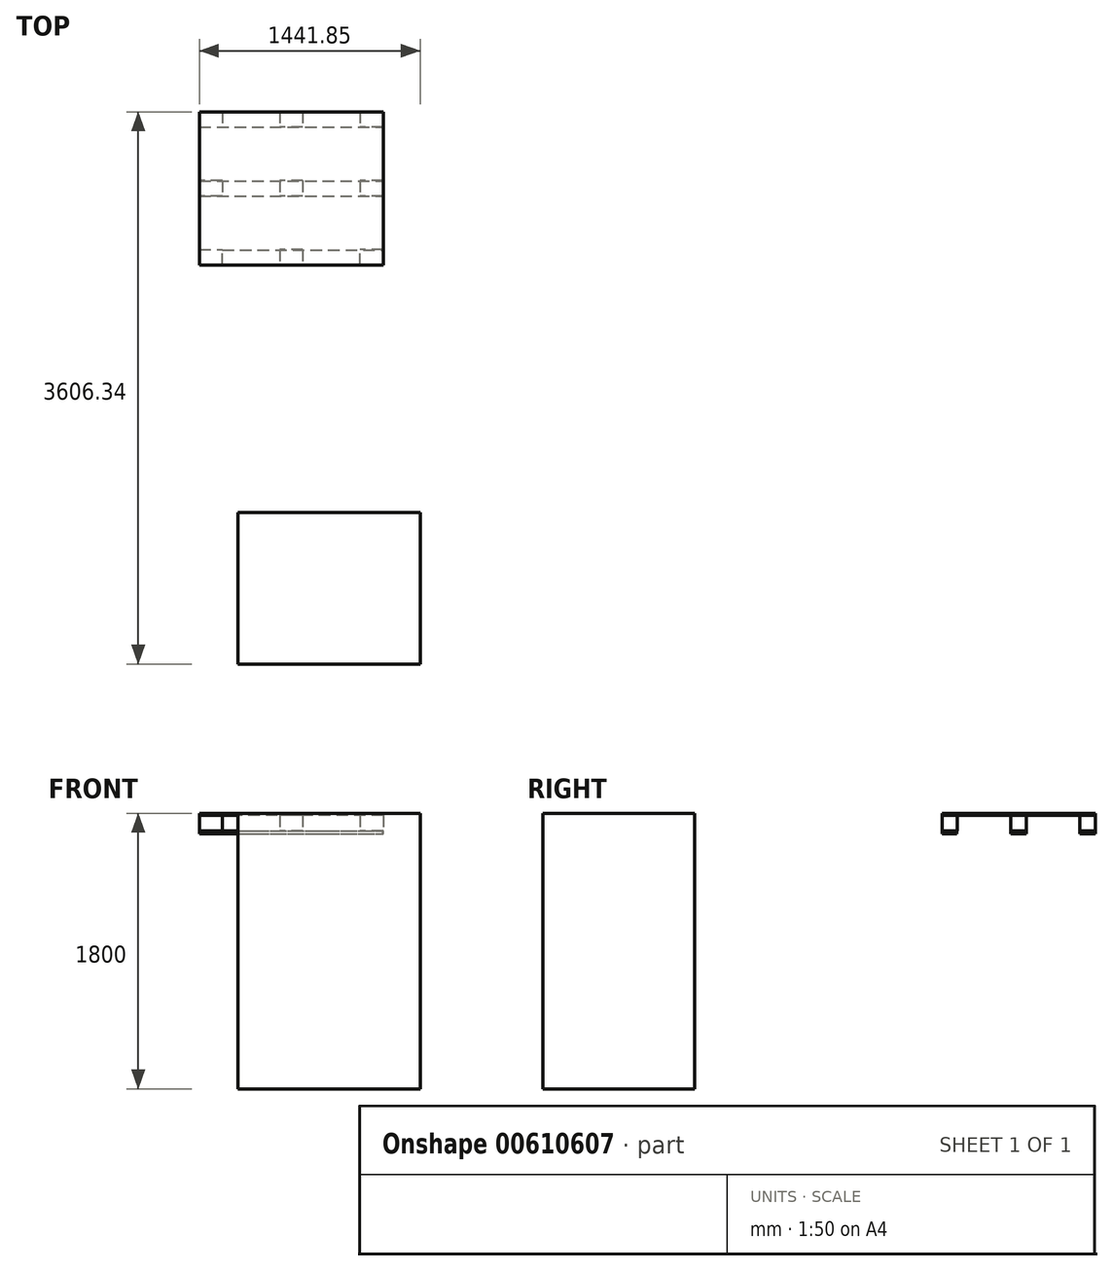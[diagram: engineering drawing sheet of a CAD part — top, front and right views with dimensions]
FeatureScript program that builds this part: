
annotation { "Feature Type Name" : "Feature", "Feature Type Description" : "" }
export const myFeature = defineFeature(function(context is Context, id is Id, definition is map)
    precondition{}
    {
        {
            var Q0;
            Q0=qCreatedBy(makeId("Top.planeOp"),FACE);
            var sketch = newSketch(context, id + "F0", { "sketchPlane" : qUnion([Q0])});
            skLineSegment(sketch, "E0.bottom", {"start": v(600, 500) * mm, "end": v(450, 500) * mm});
            skLineSegment(sketch, "E0.top", {"start": v(600, -500) * mm, "end": v(450, -500) * mm});
            skLineSegment(sketch, "E0.left", {"start": v(600, 500) * mm, "end": v(600, 400) * mm});
            skLineSegment(sketch, "E0.right", {"start": v(-600, 500) * mm, "end": v(-600, 400) * mm});
            skPoint(sketch, "E0.middle", {"position": v(0, 0) * mm});
            skLineSegment(sketch, "E1.bottom", {"start": v(-600, 500) * mm, "end": v(-450, 500) * mm});
            skLineSegment(sketch, "E1.top", {"start": v(-600, 400) * mm, "end": v(-450, 400) * mm});
            skLineSegment(sketch, "E1.right", {"start": v(-450, 500) * mm, "end": v(-450, 400) * mm});
            skLineSegment(sketch, "E2.bottom", {"start": v(-450, 50) * mm, "end": v(-600, 50) * mm});
            skLineSegment(sketch, "E2.top", {"start": v(-450, -50) * mm, "end": v(-600, -50) * mm});
            skLineSegment(sketch, "E2.left", {"start": v(-450, 50) * mm, "end": v(-450, -50) * mm});
            skPoint(sketch, "E2.middle", {"position": v(-600, 0) * mm});
            skLineSegment(sketch, "E3.bottom", {"start": v(600, 50) * mm, "end": v(450, 50) * mm});
            skLineSegment(sketch, "E3.top", {"start": v(600, -50) * mm, "end": v(450, -50) * mm});
            skLineSegment(sketch, "E3.right", {"start": v(450, 50) * mm, "end": v(450, -50) * mm});
            skPoint(sketch, "E3.middle", {"position": v(600, 0) * mm});
            skLineSegment(sketch, "E4.top", {"start": v(75, 400) * mm, "end": v(-75, 400) * mm});
            skLineSegment(sketch, "E4.left", {"start": v(75, 500) * mm, "end": v(75, 400) * mm});
            skLineSegment(sketch, "E4.right", {"start": v(-75, 500) * mm, "end": v(-75, 400) * mm});
            skPoint(sketch, "E4.middle", {"position": v(0, 500) * mm});
            skLineSegment(sketch, "E5.bottom", {"start": v(75, -400) * mm, "end": v(-75, -400) * mm});
            skLineSegment(sketch, "E5.left", {"start": v(75, -400) * mm, "end": v(75, -500) * mm});
            skLineSegment(sketch, "E5.right", {"start": v(-75, -400) * mm, "end": v(-75, -500) * mm});
            skPoint(sketch, "E5.middle", {"position": v(0, -500) * mm});
            skLineSegment(sketch, "E6.bottom", {"start": v(75, 50) * mm, "end": v(-75, 50) * mm});
            skLineSegment(sketch, "E6.top", {"start": v(75, -50) * mm, "end": v(-75, -50) * mm});
            skLineSegment(sketch, "E6.left", {"start": v(75, 50) * mm, "end": v(75, -50) * mm});
            skLineSegment(sketch, "E6.right", {"start": v(-75, 50) * mm, "end": v(-75, -50) * mm});
            skLineSegment(sketch, "E7.bottom", {"start": v(-600, -500) * mm, "end": v(-450, -500) * mm});
            skLineSegment(sketch, "E7.top", {"start": v(-600, -400) * mm, "end": v(-450, -400) * mm});
            skLineSegment(sketch, "E7.left", {"start": v(-600, -500) * mm, "end": v(-600, -400) * mm});
            skLineSegment(sketch, "E7.right", {"start": v(-450, -500) * mm, "end": v(-450, -400) * mm});
            skLineSegment(sketch, "E8.top", {"start": v(600, -400) * mm, "end": v(450, -400) * mm});
            skLineSegment(sketch, "E8.left", {"start": v(600, -500) * mm, "end": v(600, -400) * mm});
            skLineSegment(sketch, "E8.right", {"start": v(450, -500) * mm, "end": v(450, -400) * mm});
            skLineSegment(sketch, "E9.top", {"start": v(600, 400) * mm, "end": v(450, 400) * mm});
            skLineSegment(sketch, "E9.right", {"start": v(450, 500) * mm, "end": v(450, 400) * mm});
            skPoint(sketch, "E3.left.end.orphan", {"position": v(750, -50) * mm});
            skPoint(sketch, "E3.left.start.orphan", {"position": v(750, 50) * mm});
            skPoint(sketch, "E4.bottom.start.orphan", {"position": v(75, 600) * mm});
            skPoint(sketch, "E10.orphan", {"position": v(-75, 600) * mm});
            skPoint(sketch, "E2.right.start.orphan", {"position": v(-750, 50) * mm});
            skPoint(sketch, "E11.orphan", {"position": v(-750, -50) * mm});
            skPoint(sketch, "E5.top.end.orphan", {"position": v(-75, -600) * mm});
            skPoint(sketch, "E12.orphan", {"position": v(75, -600) * mm});
            skLineSegment(sketch, "E13.trimOffspring", {"start": v(-450, 500) * mm, "end": v(-600, 500) * mm});
            skLineSegment(sketch, "E14.trimOffspring", {"start": v(75, 500) * mm, "end": v(-75, 500) * mm});
            skLineSegment(sketch, "E15.trimOffspring", {"start": v(600, 50) * mm, "end": v(600, -50) * mm});
            skLineSegment(sketch, "E16.trimOffspring", {"start": v(600, -400) * mm, "end": v(600, -500) * mm});
            skLineSegment(sketch, "E17.trimOffspring", {"start": v(75, -500) * mm, "end": v(-75, -500) * mm});
            skLineSegment(sketch, "E18.trimOffspring", {"start": v(-450, -500) * mm, "end": v(-600, -500) * mm});
            skLineSegment(sketch, "E19.trimOffspring", {"start": v(-600, 50) * mm, "end": v(-600, -50) * mm});
            skLineSegment(sketch, "E20.trimOffspring", {"start": v(-600, -400) * mm, "end": v(-600, -500) * mm});
            skSolve(sketch);
        }
        {
            var Q0;
            Q0=makeQuery(id+"F0.imprint","IMPRINT",FACE,{"disambiguationData":[TD([[makeQuery(id+"F0.imprint","IMPRINT",EDGE,{"derivedFrom":sQuery(id+"F0.wireOp",EDGE,"E5.bottom")}),1.0]])]});
            var Q1;
            Q1=makeQuery(id+"F0.imprint","IMPRINT",FACE,{"disambiguationData":[TD([[makeQuery(id+"F0.imprint","IMPRINT",EDGE,{"derivedFrom":sQuery(id+"F0.wireOp",EDGE,"E7.top")}),-1.0]])]});
            var Q2;
            Q2=makeQuery(id+"F0.imprint","IMPRINT",FACE,{"disambiguationData":[TD([[makeQuery(id+"F0.imprint","IMPRINT",EDGE,{"derivedFrom":sQuery(id+"F0.wireOp",EDGE,"E2.bottom")}),1.0]])]});
            var Q3;
            Q3=makeQuery(id+"F0.imprint","IMPRINT",FACE,{"disambiguationData":[TD([[makeQuery(id+"F0.imprint","IMPRINT",EDGE,{"derivedFrom":sQuery(id+"F0.wireOp",EDGE,"E1.top")}),1.0]])]});
            var Q4;
            Q4=makeQuery(id+"F0.imprint","IMPRINT",FACE,{"disambiguationData":[TD([[makeQuery(id+"F0.imprint","IMPRINT",EDGE,{"derivedFrom":sQuery(id+"F0.wireOp",EDGE,"E4.top")}),-1.0]])]});
            var Q5;
            Q5=makeQuery(id+"F0.imprint","IMPRINT",FACE,{"disambiguationData":[TD([[makeQuery(id+"F0.imprint","IMPRINT",EDGE,{"derivedFrom":sQuery(id+"F0.wireOp",EDGE,"E6.bottom")}),1.0]])]});
            var Q6;
            Q6=makeQuery(id+"F0.imprint","IMPRINT",FACE,{"disambiguationData":[TD([[makeQuery(id+"F0.imprint","IMPRINT",EDGE,{"derivedFrom":sQuery(id+"F0.wireOp",EDGE,"E3.bottom")}),1.0]])]});
            var Q7;
            Q7=makeQuery(id+"F0.imprint","IMPRINT",FACE,{"disambiguationData":[TD([[makeQuery(id+"F0.imprint","IMPRINT",EDGE,{"derivedFrom":sQuery(id+"F0.wireOp",EDGE,"E0.bottom")}),1.0]])]});
            var Q8;
            Q8=makeQuery(id+"F0.imprint","IMPRINT",FACE,{"disambiguationData":[TD([[makeQuery(id+"F0.imprint","IMPRINT",EDGE,{"derivedFrom":sQuery(id+"F0.wireOp",EDGE,"E0.top")}),-1.0]])]});
            extrude(context, id + "F1", {"entities" : qUnion([Q0, Q1, Q2, Q3, Q4, Q5, Q6, Q7, Q8]), "depth" : 100 * mm, "offsetDistance" : 25 * mm});
        }
        {
            var Q0;
            Q0=makeQuery(id+"F1.opExtrude","CAP_FACE",FACE,{"disambiguationData":[OSD([sQuery(id+"F0.wireOp",EDGE,"E0.bottom"),sQuery(id+"F0.wireOp",EDGE,"E9.top"),sQuery(id+"F0.wireOp",EDGE,"E0.left"),sQuery(id+"F0.wireOp",EDGE,"E9.right")])],"isStart":false});
            var sketch = newSketch(context, id + "F2", { "sketchPlane" : qUnion([Q0])});
            skLineSegment(sketch, "E21.bottom", {"start": v(600, 500) * mm, "end": v(-599.99, 500) * mm});
            skLineSegment(sketch, "E21.top", {"start": v(600, -499.99) * mm, "end": v(-599.99, -499.99) * mm});
            skLineSegment(sketch, "E21.left", {"start": v(600, 500) * mm, "end": v(600, -499.99) * mm});
            skLineSegment(sketch, "E21.right", {"start": v(-599.99, 500) * mm, "end": v(-599.99, -499.99) * mm});
            skSolve(sketch);
        }
        {
            var Q0;
            {var subQ2=sQuery(id+"F2.wireOp",EDGE,"E21.top");Q0=makeQuery(id+"F2.imprint","IMPRINT",FACE,{"disambiguationData":[TD([[makeQuery(id+"F2.imprint","IMPRINT",EDGE,{"derivedFrom":subQ2}),-1.0]])]});}
            var Q1;
            {var subQ4=makeQuery(id+"F1.opExtrude","CAP_EDGE",EDGE,{"disambiguationData":[OSD([sQuery(id+"F0.wireOp",EDGE,"E9.top")])],"isStart":false});Q1=makeQuery(id+"F2.imprint","IMPRINT",FACE,{"disambiguationData":[TD([[makeQuery(id+"F2.imprint","IMPRINT",EDGE,{"derivedFrom":subQ4}),-1.0]])]});}
            extrude(context, id + "F3", {"entities" : qUnion([Q0, Q1]), "depth" : 15 * mm, "offsetDistance" : 25 * mm});
        }
        {
            var Q0;
            Q0=makeQuery(id+"F1.opExtrude","CAP_FACE",FACE,{"disambiguationData":[OSD([sQuery(id+"F0.wireOp",EDGE,"E7.top"),sQuery(id+"F0.wireOp",EDGE,"E7.right"),sQuery(id+"F0.wireOp",EDGE,"E18.trimOffspring"),sQuery(id+"F0.wireOp",EDGE,"E20.trimOffspring")])],"isStart":true});
            var sketch = newSketch(context, id + "F4", { "sketchPlane" : qUnion([Q0])});
            skLineSegment(sketch, "E22.bottom", {"start": v(-600, 500) * mm, "end": v(598.96, 500) * mm});
            skLineSegment(sketch, "E22.top", {"start": v(-600, 402.53) * mm, "end": v(598.96, 402.53) * mm});
            skLineSegment(sketch, "E22.left", {"start": v(-600, 500) * mm, "end": v(-600, 402.53) * mm});
            skLineSegment(sketch, "E22.right", {"start": v(598.96, 500) * mm, "end": v(598.96, 402.53) * mm});
            skSolve(sketch);
        }
        {
            var Q0;
            {var subQ3=sQuery(id+"F4.wireOp",EDGE,"E22.left");Q0=makeQuery(id+"F4.imprint","IMPRINT",FACE,{"disambiguationData":[TD([[makeQuery(id+"F4.imprint","IMPRINT",EDGE,{"derivedFrom":subQ3}),-1.0]])]});}
            var Q1;
            {var subQ3=sQuery(id+"F4.wireOp",EDGE,"E22.right");Q1=makeQuery(id+"F4.imprint","IMPRINT",FACE,{"disambiguationData":[TD([[makeQuery(id+"F4.imprint","IMPRINT",EDGE,{"derivedFrom":subQ3}),-1.0]])]});}
            extrude(context, id + "F5", {"entities" : qUnion([Q0, Q1]), "depth" : 20 * mm, "offsetDistance" : 25 * mm});
        }
        {
            var Q0;
            Q0=makeQuery(id+"F1.opExtrude","CAP_FACE",FACE,{"disambiguationData":[OSD([sQuery(id+"F0.wireOp",EDGE,"E1.top"),sQuery(id+"F0.wireOp",EDGE,"E0.right"),sQuery(id+"F0.wireOp",EDGE,"E1.right"),sQuery(id+"F0.wireOp",EDGE,"E13.trimOffspring")])],"isStart":true});
            var sketch = newSketch(context, id + "F6", { "sketchPlane" : qUnion([Q0])});
            skLineSegment(sketch, "E23.bottom", {"start": v(-600, -500) * mm, "end": v(597.73, -500) * mm});
            skLineSegment(sketch, "E23.top", {"start": v(-600, -400.93) * mm, "end": v(597.73, -400.93) * mm});
            skLineSegment(sketch, "E23.left", {"start": v(-600, -500) * mm, "end": v(-600, -400.93) * mm});
            skLineSegment(sketch, "E23.right", {"start": v(597.73, -500) * mm, "end": v(597.73, -400.93) * mm});
            skLineSegment(sketch, "E24.bottom", {"start": v(-600, -48.82) * mm, "end": v(599.89, -48.82) * mm});
            skLineSegment(sketch, "E24.top", {"start": v(-600, 49.95) * mm, "end": v(599.89, 49.95) * mm});
            skLineSegment(sketch, "E24.left", {"start": v(-600, -48.82) * mm, "end": v(-600, 49.95) * mm});
            skLineSegment(sketch, "E24.right", {"start": v(599.89, -48.82) * mm, "end": v(599.89, 49.95) * mm});
            skSolve(sketch);
        }
        {
            var Q0;
            Q0=makeQuery(id+"F6.imprint","IMPRINT",FACE,{"disambiguationData":[TD([[makeQuery(id+"F6.imprint","IMPRINT",EDGE,{"derivedFrom":sQuery(id+"F6.wireOp",EDGE,"E24.bottom")}),1.0]])]});
            var Q1;
            {var subQ3=sQuery(id+"F6.wireOp",EDGE,"E23.right");Q1=makeQuery(id+"F6.imprint","IMPRINT",FACE,{"disambiguationData":[TD([[makeQuery(id+"F6.imprint","IMPRINT",EDGE,{"derivedFrom":subQ3}),1.0]])]});}
            var Q2;
            {var subQ0=sQuery(id+"F6.wireOp",EDGE,"E23.left");Q2=makeQuery(id+"F6.imprint","IMPRINT",FACE,{"disambiguationData":[TD([[makeQuery(id+"F6.imprint","IMPRINT",EDGE,{"derivedFrom":subQ0}),-1.0]])]});}
            extrude(context, id + "F7", {"entities" : qUnion([Q0, Q1, Q2]), "depth" : 20 * mm, "offsetDistance" : 25 * mm});
        }
        {
            var Q0;
            Q0=makeQuery(id+"F3.opExtrude","CAP_FACE",FACE,{"disambiguationData":[OSD([sQuery(id+"F2.wireOp",EDGE,"E21.bottom"),sQuery(id+"F2.wireOp",EDGE,"E21.top"),sQuery(id+"F2.wireOp",EDGE,"E21.left"),sQuery(id+"F2.wireOp",EDGE,"E21.right")])],"isStart":false});
            var sketch = newSketch(context, id + "F8", { "sketchPlane" : qUnion([Q0])});
            skLineSegment(sketch, "E25.bottom", {"start": v(841.85, -2116.34) * mm, "end": v(-348.15, -2116.34) * mm});
            skLineSegment(sketch, "E25.top", {"start": v(841.85, -3106.34) * mm, "end": v(-348.15, -3106.34) * mm});
            skLineSegment(sketch, "E25.left", {"start": v(841.85, -2116.34) * mm, "end": v(841.85, -3106.34) * mm});
            skLineSegment(sketch, "E25.right", {"start": v(-348.15, -2116.34) * mm, "end": v(-348.15, -3106.34) * mm});
            skSolve(sketch);
        }
        {
            var Q0;
            Q0 = qSketchRegion(id + "F8", true);
            extrude(context, id + "F9", {"entities" : qUnion([Q0]), "oppositeDirection" : true, "depth" : 1800 * mm, "offsetDistance" : 25 * mm});
        }
    });
